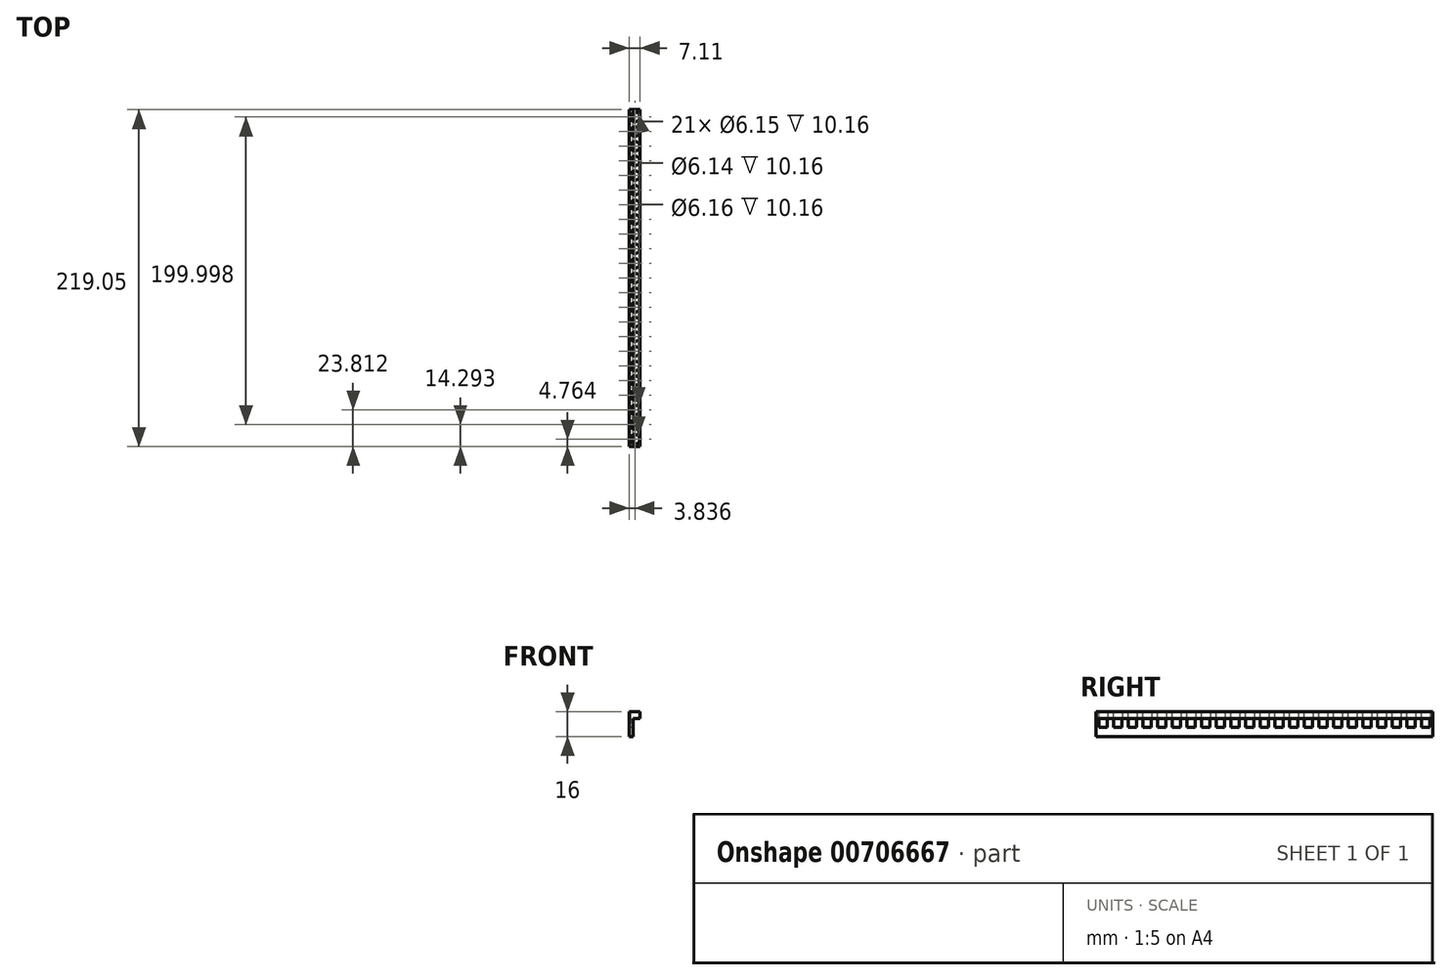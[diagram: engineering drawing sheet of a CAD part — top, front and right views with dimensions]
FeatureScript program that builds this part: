
annotation { "Feature Type Name" : "Feature", "Feature Type Description" : "" }
export const myFeature = defineFeature(function(context is Context, id is Id, definition is map)
    precondition{}
    {
        {
            var Q0;
            Q0=qCreatedBy(makeId("Top.planeOp"),FACE);
            var sketch = newSketch(context, id + "F0", { "sketchPlane" : qUnion([Q0])});
            skLineSegment(sketch, "E0.bottom", {"start": v(-28.72, 173.5) * mm, "end": v(-21.6, 173.5) * mm});
            skLineSegment(sketch, "E0.top", {"start": v(-28.72, -48.75) * mm, "end": v(-21.6, -48.75) * mm});
            skLineSegment(sketch, "E0.left", {"start": v(-28.72, 173.5) * mm, "end": v(-28.72, -48.75) * mm});
            skLineSegment(sketch, "E0.right", {"start": v(-21.6, 173.5) * mm, "end": v(-21.6, -48.75) * mm});
            skCircle(sketch, "E1", {"center": v(-24.88, -43.99) * mm, "radius": 3.08 * mm});
            skCircle(sketch, "E2", {"center": v(-24.88, -34.46) * mm, "radius": 3.07 * mm});
            skCircle(sketch, "E3", {"center": v(-24.88, -24.94) * mm, "radius": 3.07 * mm});
            skCircle(sketch, "E4", {"center": v(-24.88, -15.41) * mm, "radius": 3.07 * mm});
            skCircle(sketch, "E5", {"center": v(-24.88, -5.9) * mm, "radius": 3.07 * mm});
            skCircle(sketch, "E6", {"center": v(-24.88, 3.63) * mm, "radius": 3.07 * mm});
            skCircle(sketch, "E7", {"center": v(-24.88, 13.16) * mm, "radius": 3.07 * mm});
            skCircle(sketch, "E8", {"center": v(-24.88, 22.68) * mm, "radius": 3.07 * mm});
            skCircle(sketch, "E9", {"center": v(-24.88, 32.2) * mm, "radius": 3.07 * mm});
            skCircle(sketch, "E10", {"center": v(-24.88, 41.73) * mm, "radius": 3.07 * mm});
            skCircle(sketch, "E11", {"center": v(-24.88, 51.26) * mm, "radius": 3.07 * mm});
            skCircle(sketch, "E12", {"center": v(-24.88, 60.78) * mm, "radius": 3.07 * mm});
            skCircle(sketch, "E13", {"center": v(-24.88, 70.3) * mm, "radius": 3.07 * mm});
            skCircle(sketch, "E14", {"center": v(-24.88, 79.82) * mm, "radius": 3.07 * mm});
            skCircle(sketch, "E15", {"center": v(-24.88, 89.35) * mm, "radius": 3.07 * mm});
            skCircle(sketch, "E16", {"center": v(-24.88, 98.87) * mm, "radius": 3.07 * mm});
            skCircle(sketch, "E17", {"center": v(-24.88, 108.4) * mm, "radius": 3.07 * mm});
            skCircle(sketch, "E18", {"center": v(-24.88, 117.92) * mm, "radius": 3.07 * mm});
            skCircle(sketch, "E19", {"center": v(-24.88, 127.45) * mm, "radius": 3.07 * mm});
            skCircle(sketch, "E20", {"center": v(-24.88, 136.97) * mm, "radius": 3.07 * mm});
            skCircle(sketch, "E21", {"center": v(-24.88, 146.5) * mm, "radius": 3.07 * mm});
            skCircle(sketch, "E22", {"center": v(-24.88, 156.02) * mm, "radius": 3.07 * mm});
            skCircle(sketch, "E23", {"center": v(-24.88, 165.54) * mm, "radius": 3.07 * mm});
            skLineSegment(sketch, "E24", {"start": v(-26.08, -47.79) * mm, "end": v(-26.08, -48.75) * mm});
            skLineSegment(sketch, "E25", {"start": v(-26.08, -48.75) * mm, "end": v(-26.08, 173.5) * mm});
            skSolve(sketch);
        }
        {
            var Q0;
            {var subQ32=sQuery(id+"F0.wireOp",EDGE,"E0.right");Q0=makeQuery(id+"F0.imprint","IMPRINT",FACE,{"disambiguationData":[TD([[makeQuery(id+"F0.imprint","IMPRINT",EDGE,{"derivedFrom":subQ32}),-1.0]])]});}
            extrude(context, id + "F1", {"entities" : qUnion([Q0]), "depth" : 4.32 * mm});
        }
        {
            var Q0;
            {var subQ36=sQuery(id+"F0.wireOp",EDGE,"E0.left");Q0=makeQuery(id+"F0.imprint","IMPRINT",FACE,{"disambiguationData":[TD([[makeQuery(id+"F0.imprint","IMPRINT",EDGE,{"derivedFrom":subQ36}),1.0]])]});}
            extrude(context, id + "F2", {"entities" : qUnion([Q0]), "operationType" : NewBodyOperationType.ADD, "depth" : 4.32 * mm});
        }
        {
            var Q0;
            {var subQ36=sQuery(id+"F0.wireOp",EDGE,"E0.left");Q0=makeQuery(id+"F0.imprint","IMPRINT",FACE,{"disambiguationData":[TD([[makeQuery(id+"F0.imprint","IMPRINT",EDGE,{"derivedFrom":subQ36}),1.0]])]});}
            extrude(context, id + "F3", {"entities" : qUnion([Q0]), "operationType" : NewBodyOperationType.ADD, "oppositeDirection" : true, "depth" : 5.84 * mm});
        }
        {
            var Q0;
            Q0=makeQuery(id+"F3.opExtrude","CAP_FACE",FACE,{"disambiguationData":[OSD([sQuery(id+"F0.wireOp",EDGE,"E0.bottom"),sQuery(id+"F0.wireOp",EDGE,"E0.top"),sQuery(id+"F0.wireOp",EDGE,"E0.left"),sQuery(id+"F0.wireOp",EDGE,"E1"),sQuery(id+"F0.wireOp",EDGE,"E2"),sQuery(id+"F0.wireOp",EDGE,"E3"),sQuery(id+"F0.wireOp",EDGE,"E4"),sQuery(id+"F0.wireOp",EDGE,"E5"),sQuery(id+"F0.wireOp",EDGE,"E6"),sQuery(id+"F0.wireOp",EDGE,"E7"),sQuery(id+"F0.wireOp",EDGE,"E8"),sQuery(id+"F0.wireOp",EDGE,"E9"),sQuery(id+"F0.wireOp",EDGE,"E10"),sQuery(id+"F0.wireOp",EDGE,"E11"),sQuery(id+"F0.wireOp",EDGE,"E12"),sQuery(id+"F0.wireOp",EDGE,"E13"),sQuery(id+"F0.wireOp",EDGE,"E14"),sQuery(id+"F0.wireOp",EDGE,"E15"),sQuery(id+"F0.wireOp",EDGE,"E16"),sQuery(id+"F0.wireOp",EDGE,"E17"),sQuery(id+"F0.wireOp",EDGE,"E18"),sQuery(id+"F0.wireOp",EDGE,"E19"),sQuery(id+"F0.wireOp",EDGE,"E20"),sQuery(id+"F0.wireOp",EDGE,"E21"),sQuery(id+"F0.wireOp",EDGE,"E22"),sQuery(id+"F0.wireOp",EDGE,"E23"),sQuery(id+"F0.wireOp",EDGE,"E25")])],"isStart":false});
            var sketch = newSketch(context, id + "F4", { "sketchPlane" : qUnion([Q0])});
            skLineSegment(sketch, "E26.bottom", {"start": v(-28.72, -173.5) * mm, "end": v(-26.08, -173.5) * mm});
            skLineSegment(sketch, "E26.top", {"start": v(-28.72, 48.75) * mm, "end": v(-26.08, 48.75) * mm});
            skLineSegment(sketch, "E26.left", {"start": v(-28.72, -173.5) * mm, "end": v(-28.72, 48.75) * mm});
            skLineSegment(sketch, "E26.right", {"start": v(-26.08, -173.5) * mm, "end": v(-26.08, 48.75) * mm});
            skSolve(sketch);
        }
        {
            var Q0;
            Q0=qSketchRegion(id+"F4",true);
            extrude(context, id + "F5", {"entities" : qUnion([Q0]), "operationType" : NewBodyOperationType.ADD, "depth" : 5.84 * mm});
        }
        {
            var Q0;
            {var subQ0=sQuery(id+"F0.wireOp",EDGE,"E0.top");Q0=makeQuery(id+"F5.boolean.opBoolean","MERGE",FACE,{"derivedFrom":[makeQuery(id+"F3.boolean.opBoolean","MERGE",FACE,{"derivedFrom":[makeQuery(id+"F2.boolean.opBoolean","MERGE",FACE,{"derivedFrom":[makeQuery(id+"F1.opExtrude","SWEPT_FACE",FACE,{"disambiguationData":[OSD([subQ0])]}),makeQuery(id+"F2.opExtrude","SWEPT_FACE",FACE,{"disambiguationData":[OSD([subQ0])]})]}),makeQuery(id+"F3.opExtrude","SWEPT_FACE",FACE,{"disambiguationData":[OSD([subQ0])]})]}),makeQuery(id+"F5.opExtrude","SWEPT_FACE",FACE,{"disambiguationData":[OSD([sQuery(id+"F4.wireOp",EDGE,"E26.top")])]})]});}
            extrude(context, id + "F6", {"entities" : qUnion([Q0]), "operationType" : NewBodyOperationType.ADD, "depth" : 0 * mm});
        }
        {
            var Q0;
            {var subQ0=sQuery(id+"F0.wireOp",EDGE,"E0.bottom");Q0=makeQuery(id+"F5.boolean.opBoolean","MERGE",FACE,{"derivedFrom":[makeQuery(id+"F3.boolean.opBoolean","MERGE",FACE,{"derivedFrom":[makeQuery(id+"F2.boolean.opBoolean","MERGE",FACE,{"derivedFrom":[makeQuery(id+"F1.opExtrude","SWEPT_FACE",FACE,{"disambiguationData":[OSD([subQ0])]}),makeQuery(id+"F2.opExtrude","SWEPT_FACE",FACE,{"disambiguationData":[OSD([subQ0])]})]}),makeQuery(id+"F3.opExtrude","SWEPT_FACE",FACE,{"disambiguationData":[OSD([subQ0])]})]}),makeQuery(id+"F5.opExtrude","SWEPT_FACE",FACE,{"disambiguationData":[OSD([sQuery(id+"F4.wireOp",EDGE,"E26.bottom")])]})]});}
            extrude(context, id + "F7", {"entities" : qUnion([Q0]), "operationType" : NewBodyOperationType.REMOVE, "oppositeDirection" : true, "depth" : 3.2 * mm});
        }
    });
